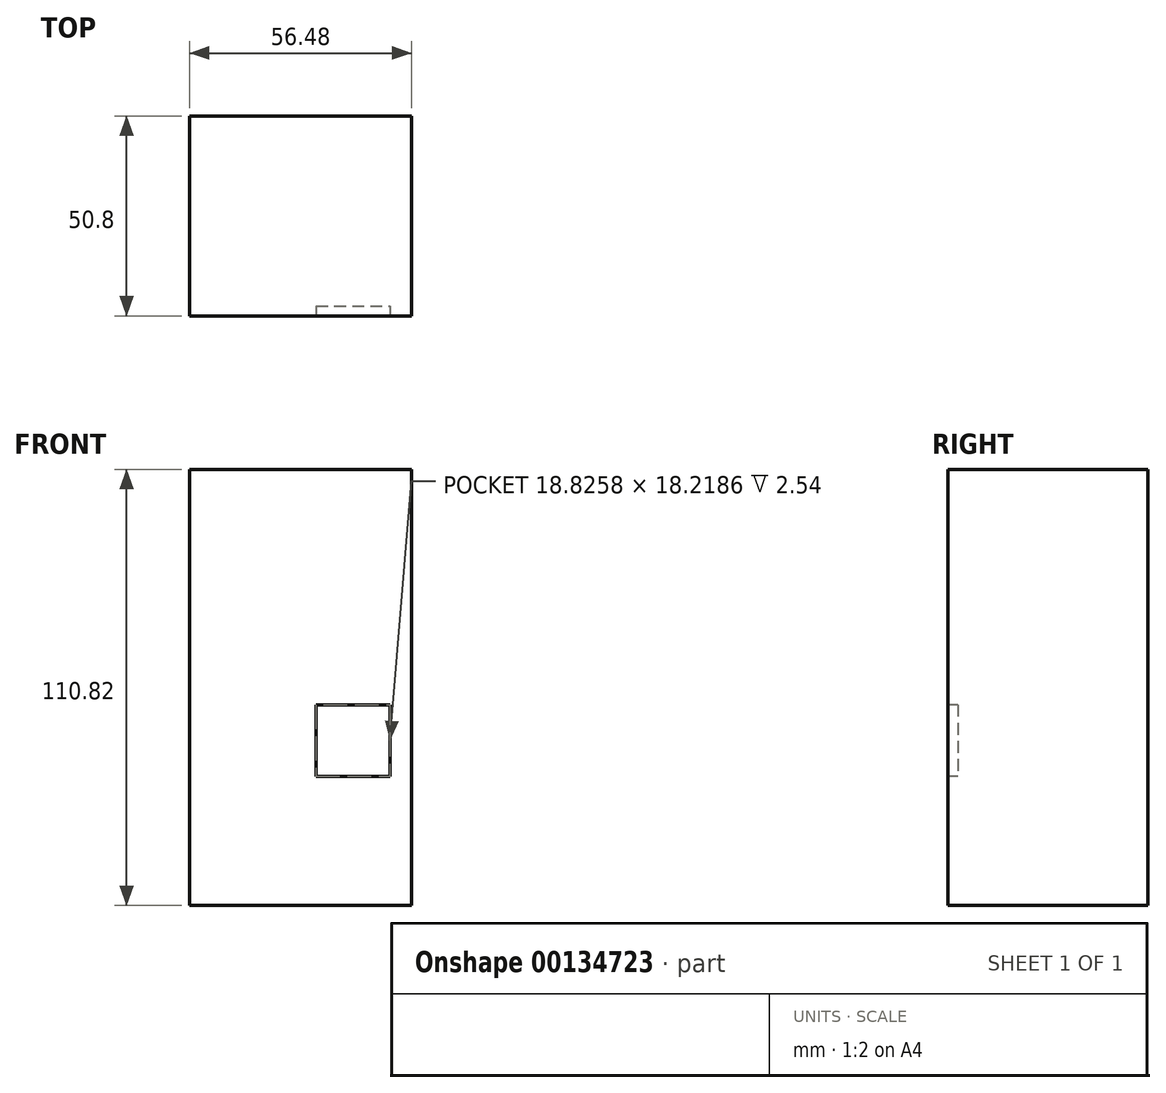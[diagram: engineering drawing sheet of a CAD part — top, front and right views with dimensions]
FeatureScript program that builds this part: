
annotation { "Feature Type Name" : "Feature", "Feature Type Description" : "" }
export const myFeature = defineFeature(function(context is Context, id is Id, definition is map)
    precondition{}
    {
        {
            var Q0;
            Q0=qCreatedBy(makeId("Front.planeOp"),FACE);
            var sketch = newSketch(context, id + "F0", { "sketchPlane" : qUnion([Q0])});
            skLineSegment(sketch, "E0.bottom", {"start": v(-28.24, 55.41) * mm, "end": v(28.24, 55.41) * mm});
            skLineSegment(sketch, "E0.top", {"start": v(-28.24, -55.41) * mm, "end": v(28.24, -55.41) * mm});
            skLineSegment(sketch, "E0.left", {"start": v(-28.24, 55.41) * mm, "end": v(-28.24, -55.41) * mm});
            skLineSegment(sketch, "E0.right", {"start": v(28.24, 55.41) * mm, "end": v(28.24, -55.41) * mm});
            skPoint(sketch, "E0.middle", {"position": v(0, 0) * mm});
            skSolve(sketch);
        }
        {
            var Q0;
            Q0=makeQuery(id+"F0.imprint","IMPRINT",FACE,{"disambiguationData":[TD([[makeQuery(id+"F0.imprint","IMPRINT",EDGE,{"derivedFrom":sQuery(id+"F0.wireOp",EDGE,"E0.bottom")}),-1.0]])]});
            extrude(context, id + "F1", {"entities" : qUnion([Q0]), "depth" : 50.8 * mm});
        }
        {
            var Q0;
            Q0=makeQuery(id+"F1.opExtrude","CAP_FACE",FACE,{"disambiguationData":[OSD([sQuery(id+"F0.wireOp",EDGE,"E0.bottom"),sQuery(id+"F0.wireOp",EDGE,"E0.top"),sQuery(id+"F0.wireOp",EDGE,"E0.left"),sQuery(id+"F0.wireOp",EDGE,"E0.right")])],"isStart":false});
            var sketch = newSketch(context, id + "F2", { "sketchPlane" : qUnion([Q0])});
            skText(sketch, "E1", { "text": "Police Public Call Box", "fontName": "NotoSerif-Regular.ttf"});
            skLineSegment(sketch, "E2.bottom", {"start": v(-6.98, 63.92) * mm, "end": v(6.68, 63.92) * mm});
            skLineSegment(sketch, "E2.top", {"start": v(-6.98, 55.41) * mm, "end": v(6.68, 55.41) * mm});
            skLineSegment(sketch, "E2.left", {"start": v(-6.98, 63.92) * mm, "end": v(-6.98, 55.41) * mm});
            skLineSegment(sketch, "E2.right", {"start": v(6.68, 63.92) * mm, "end": v(6.68, 55.41) * mm});
            skLineSegment(sketch, "E3", {"start": v(-25.8, 51.45) * mm, "end": v(-25.8, -55.41) * mm});
            skLineSegment(sketch, "E4", {"start": v(25.5, 51.45) * mm, "end": v(25.5, -55.41) * mm});
            skLineSegment(sketch, "E5", {"start": v(-25.8, -52.38) * mm, "end": v(25.5, -52.38) * mm});
            skLineSegment(sketch, "E6.bottom", {"start": v(-23.08, 46.91) * mm, "end": v(-2.73, 46.91) * mm});
            skLineSegment(sketch, "E6.top", {"start": v(-23.08, 29.6) * mm, "end": v(-2.73, 29.6) * mm});
            skLineSegment(sketch, "E6.left", {"start": v(-23.08, 46.91) * mm, "end": v(-23.08, 29.6) * mm});
            skLineSegment(sketch, "E6.right", {"start": v(-2.73, 46.91) * mm, "end": v(-2.73, 29.6) * mm});
            skLineSegment(sketch, "E7.bottom", {"start": v(3.04, 46.91) * mm, "end": v(22.47, 46.91) * mm});
            skLineSegment(sketch, "E7.top", {"start": v(3.04, 29.6) * mm, "end": v(22.47, 29.6) * mm});
            skLineSegment(sketch, "E7.left", {"start": v(3.04, 46.91) * mm, "end": v(3.04, 29.6) * mm});
            skLineSegment(sketch, "E7.right", {"start": v(22.47, 46.91) * mm, "end": v(22.47, 29.6) * mm});
            const initialGuessF2  = {"E1": [-0.02824, 0.05145, 1, 0, 0.00396]};
            skSetInitialGuess(sketch, initialGuessF2);
            skSolve(sketch);
        }
        {
            var Q0;
            Q0=makeQuery(id+"F2.imprint","IMPRINT",FACE,{"disambiguationData":[TD([[makeQuery(id+"F2.imprint","IMPRINT",EDGE,{"derivedFrom":sQuery(id+"F2.wireOp",EDGE,"E1.sketch_text.stroke-0")}),1.0]])]});
            var sketch = newSketch(context, id + "F3", { "sketchPlane" : qUnion([Q0])});
            skLineSegment(sketch, "E8.bottom", {"start": v(-22.17, 22.93) * mm, "end": v(-3.04, 22.93) * mm});
            skLineSegment(sketch, "E8.top", {"start": v(-22.17, 4.1) * mm, "end": v(-3.04, 4.1) * mm});
            skLineSegment(sketch, "E8.left", {"start": v(-22.17, 22.93) * mm, "end": v(-22.17, 4.1) * mm});
            skLineSegment(sketch, "E8.right", {"start": v(-3.04, 22.93) * mm, "end": v(-3.04, 4.1) * mm});
            skPoint(sketch, "E9.oppositeSnap0", {"position": v(-12.6, 4.1) * mm});
            skLineSegment(sketch, "E9.bottom", {"start": v(3.04, 23.23) * mm, "end": v(22.77, 23.23) * mm});
            skLineSegment(sketch, "E9.top", {"start": v(3.04, 4.1) * mm, "end": v(22.77, 4.1) * mm});
            skLineSegment(sketch, "E9.left", {"start": v(3.04, 23.23) * mm, "end": v(3.04, 4.1) * mm});
            skLineSegment(sketch, "E9.right", {"start": v(22.77, 23.23) * mm, "end": v(22.77, 4.1) * mm});
            skLineSegment(sketch, "E10", {"start": v(-17.61, 46) * mm, "end": v(-17.61, 29) * mm});
            skLineSegment(sketch, "E11", {"start": v(-9.72, 46.3) * mm, "end": v(-9.72, 29.6) * mm});
            skLineSegment(sketch, "E12", {"start": v(-23.08, 37.5) * mm, "end": v(-3.34, 37.5) * mm});
            skPoint(sketch, "E12.endSnap0", {"position": v(-17.61, 37.5) * mm});
            skLineSegment(sketch, "E13", {"start": v(3.04, 38.41) * mm, "end": v(21.86, 38.41) * mm});
            skLineSegment(sketch, "E14", {"start": v(7.9, 46.6) * mm, "end": v(7.9, 30.21) * mm});
            skLineSegment(sketch, "E15", {"start": v(16.1, 46.6) * mm, "end": v(16.1, 29.9) * mm});
            skLineSegment(sketch, "E16.bottom", {"start": v(-19.13, 18.98) * mm, "end": v(-6.07, 18.98) * mm});
            skLineSegment(sketch, "E16.top", {"start": v(-19.13, 7.44) * mm, "end": v(-6.07, 7.44) * mm});
            skLineSegment(sketch, "E16.left", {"start": v(-19.13, 18.98) * mm, "end": v(-19.13, 7.44) * mm});
            skLineSegment(sketch, "E16.right", {"start": v(-6.07, 18.98) * mm, "end": v(-6.07, 7.44) * mm});
            skLineSegment(sketch, "E17.bottom", {"start": v(-22.17, -4.1) * mm, "end": v(-3.64, -4.1) * mm});
            skLineSegment(sketch, "E17.top", {"start": v(-22.17, -22.01) * mm, "end": v(-3.64, -22.01) * mm});
            skLineSegment(sketch, "E17.left", {"start": v(-22.17, -4.1) * mm, "end": v(-22.17, -22.01) * mm});
            skLineSegment(sketch, "E17.right", {"start": v(-3.64, -4.1) * mm, "end": v(-3.64, -22.01) * mm});
            skLineSegment(sketch, "E18.bottom", {"start": v(3.95, -4.4) * mm, "end": v(22.77, -4.4) * mm});
            skLineSegment(sketch, "E18.top", {"start": v(3.95, -22.62) * mm, "end": v(22.77, -22.62) * mm});
            skLineSegment(sketch, "E18.left", {"start": v(3.95, -4.4) * mm, "end": v(3.95, -22.62) * mm});
            skLineSegment(sketch, "E18.right", {"start": v(22.77, -4.4) * mm, "end": v(22.77, -22.62) * mm});
            skLineSegment(sketch, "E19.bottom", {"start": v(-22.17, -29.9) * mm, "end": v(-3.04, -29.9) * mm});
            skLineSegment(sketch, "E19.top", {"start": v(-22.17, -48.43) * mm, "end": v(-3.04, -48.43) * mm});
            skLineSegment(sketch, "E19.left", {"start": v(-22.17, -29.9) * mm, "end": v(-22.17, -48.43) * mm});
            skLineSegment(sketch, "E19.right", {"start": v(-3.04, -29.9) * mm, "end": v(-3.04, -48.43) * mm});
            skLineSegment(sketch, "E20.bottom", {"start": v(3.04, -30.82) * mm, "end": v(22.17, -30.82) * mm});
            skLineSegment(sketch, "E20.top", {"start": v(3.04, -48.13) * mm, "end": v(22.17, -48.13) * mm});
            skLineSegment(sketch, "E20.left", {"start": v(3.04, -30.82) * mm, "end": v(3.04, -48.13) * mm});
            skLineSegment(sketch, "E20.right", {"start": v(22.17, -30.82) * mm, "end": v(22.17, -48.13) * mm});
            skLineSegment(sketch, "E21", {"start": v(-4.86, 63.61) * mm, "end": v(-4.86, 55.41) * mm});
            skLineSegment(sketch, "E22", {"start": v(0, 63.61) * mm, "end": v(0, 55.41) * mm});
            skLineSegment(sketch, "E23", {"start": v(3.95, 63.61) * mm, "end": v(3.95, 56.02) * mm});
            skLineSegment(sketch, "E24", {"start": v(-6.68, 59.36) * mm, "end": v(6.68, 59.82) * mm});
            skPoint(sketch, "E24.endSnap0", {"position": v(3.95, 59.82) * mm});
            skSolve(sketch);
        }
        {
            var Q0;
            Q0=makeQuery(id+"F3.imprint","IMPRINT",FACE,{"disambiguationData":[TD([[makeQuery(id+"F3.imprint","IMPRINT",EDGE,{"derivedFrom":sQuery(id+"F3.wireOp",EDGE,"E18.bottom")}),-1.0]])]});
            extrude(context, id + "F4", {"entities" : qUnion([Q0]), "operationType" : NewBodyOperationType.REMOVE, "oppositeDirection" : true, "depth" : 2.54 * mm});
        }
    });
